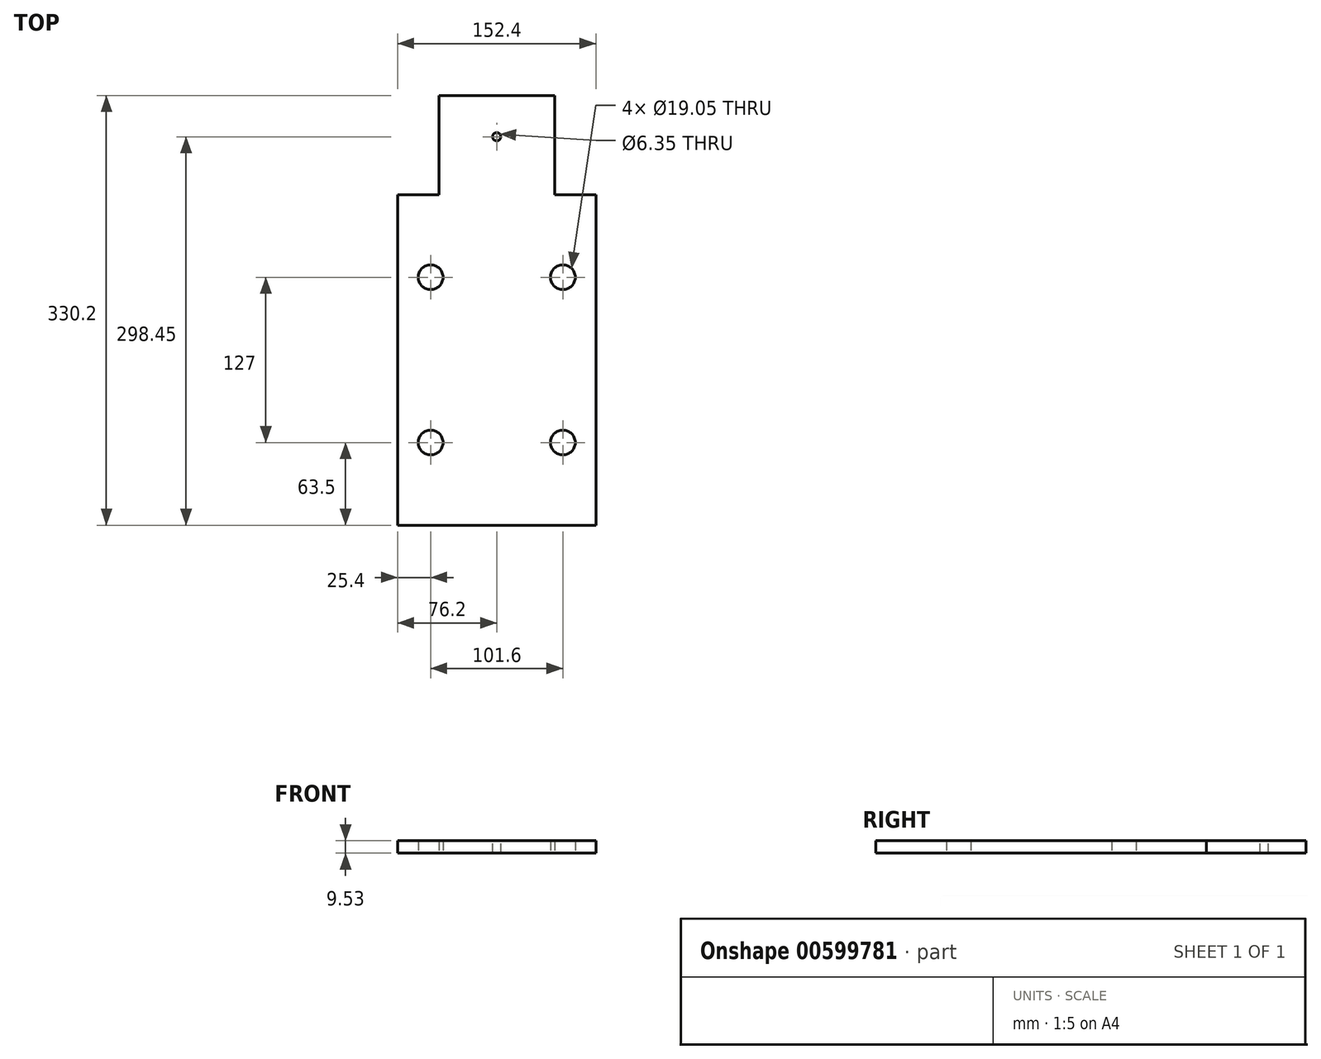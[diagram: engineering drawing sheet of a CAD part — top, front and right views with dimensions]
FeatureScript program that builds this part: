
annotation { "Feature Type Name" : "Feature", "Feature Type Description" : "" }
export const myFeature = defineFeature(function(context is Context, id is Id, definition is map)
    precondition{}
    {
        {
            var Q0;
            Q0=qCreatedBy(makeId("Top.planeOp"),FACE);
            var sketch = newSketch(context, id + "F0", { "sketchPlane" : qUnion([Q0])});
            skLineSegment(sketch, "E0.bottom", {"start": v(76.2, 127) * mm, "end": v(-76.2, 127) * mm});
            skLineSegment(sketch, "E0.top", {"start": v(76.2, -127) * mm, "end": v(-76.2, -127) * mm});
            skLineSegment(sketch, "E0.left", {"start": v(76.2, 127) * mm, "end": v(76.2, -127) * mm});
            skLineSegment(sketch, "E0.right", {"start": v(-76.2, 127) * mm, "end": v(-76.2, -127) * mm});
            skPoint(sketch, "E0.middle", {"position": v(0, 0) * mm});
            skLineSegment(sketch, "E1", {"start": v(-76.2, 0) * mm, "end": v(76.2, 0) * mm, "construction": true});
            skLineSegment(sketch, "E2", {"start": v(0, 127) * mm, "end": v(0, -127) * mm, "construction": true});
            skLineSegment(sketch, "E3", {"start": v(-50.8, 63.5) * mm, "end": v(-50.8, -63.5) * mm, "construction": true});
            skPoint(sketch, "E4", {"position": v(-50.8, 0) * mm});
            skCircle(sketch, "E5", {"center": v(-50.8, -63.5) * mm, "radius": 9.53 * mm});
            skCircle(sketch, "E6", {"center": v(-50.8, 63.5) * mm, "radius": 9.53 * mm});
            skCircle(sketch, "E7.MirrorC", {"center": v(50.8, 63.5) * mm, "radius": 9.53 * mm});
            skCircle(sketch, "E8.MirrorC", {"center": v(50.8, -63.5) * mm, "radius": 9.53 * mm});
            skSolve(sketch);
        }
        {
            var Q0;
            Q0=qSketchRegion(id+"F0",true);
            extrude(context, id + "F1", {"entities" : qUnion([Q0]), "depth" : 9.52 * mm, "offsetDistance" : 25.4 * mm});
        }
        {
            var Q0;
            Q0=makeQuery(id+"F1.opExtrude","SWEPT_FACE",FACE,{"disambiguationData":[OSD([sQuery(id+"F0.wireOp",EDGE,"E0.bottom")])]});
            var sketch = newSketch(context, id + "F2", { "sketchPlane" : qUnion([Q0])});
            skLineSegment(sketch, "E9.bottom", {"start": v(44.45, 9.53) * mm, "end": v(-44.45, 9.53) * mm});
            skLineSegment(sketch, "E9.top", {"start": v(44.45, 0) * mm, "end": v(-44.45, 0) * mm});
            skLineSegment(sketch, "E9.left", {"start": v(44.45, 9.53) * mm, "end": v(44.45, 0) * mm});
            skLineSegment(sketch, "E9.right", {"start": v(-44.45, 9.52) * mm, "end": v(-44.45, 0) * mm});
            skSolve(sketch);
        }
        {
            var Q0;
            Q0 = qSketchRegion(id + "F2", true);
            extrude(context, id + "F3", {"entities" : qUnion([Q0]), "operationType" : NewBodyOperationType.ADD, "depth" : 76.2 * mm, "offsetDistance" : 25.4 * mm});
        }
        {
            var Q0;
            Q0=makeQuery(id+"F3.boolean.opBoolean","MERGE",FACE,{"derivedFrom":[makeQuery(id+"F1.opExtrude","CAP_FACE",FACE,{"disambiguationData":[OSD([sQuery(id+"F0.wireOp",EDGE,"E0.bottom"),sQuery(id+"F0.wireOp",EDGE,"E0.top"),sQuery(id+"F0.wireOp",EDGE,"E0.left"),sQuery(id+"F0.wireOp",EDGE,"E0.right"),sQuery(id+"F0.wireOp",EDGE,"E5"),sQuery(id+"F0.wireOp",EDGE,"E6"),sQuery(id+"F0.wireOp",EDGE,"E7.MirrorC"),sQuery(id+"F0.wireOp",EDGE,"E8.MirrorC")])],"isStart":false}),makeQuery(id+"F3.opExtrude","SWEPT_FACE",FACE,{"disambiguationData":[OSD([sQuery(id+"F2.wireOp",EDGE,"E9.bottom")])]})]});
            var sketch = newSketch(context, id + "F4", { "sketchPlane" : qUnion([Q0])});
            skLineSegment(sketch, "E10", {"start": v(-44.45, 171.45) * mm, "end": v(44.45, 171.45) * mm, "construction": true});
            skCircle(sketch, "E11", {"center": v(0, 171.45) * mm, "radius": 3.18 * mm});
            skSolve(sketch);
        }
        {
            var Q0;
            Q0 = qSketchRegion(id + "F4", true);
            extrude(context, id + "F5", {"entities" : qUnion([Q0]), "operationType" : NewBodyOperationType.REMOVE, "endBound" : BoundingType.THROUGH_ALL, "oppositeDirection" : true, "depth" : 25.4 * mm, "offsetDistance" : 25.4 * mm});
        }
    });
